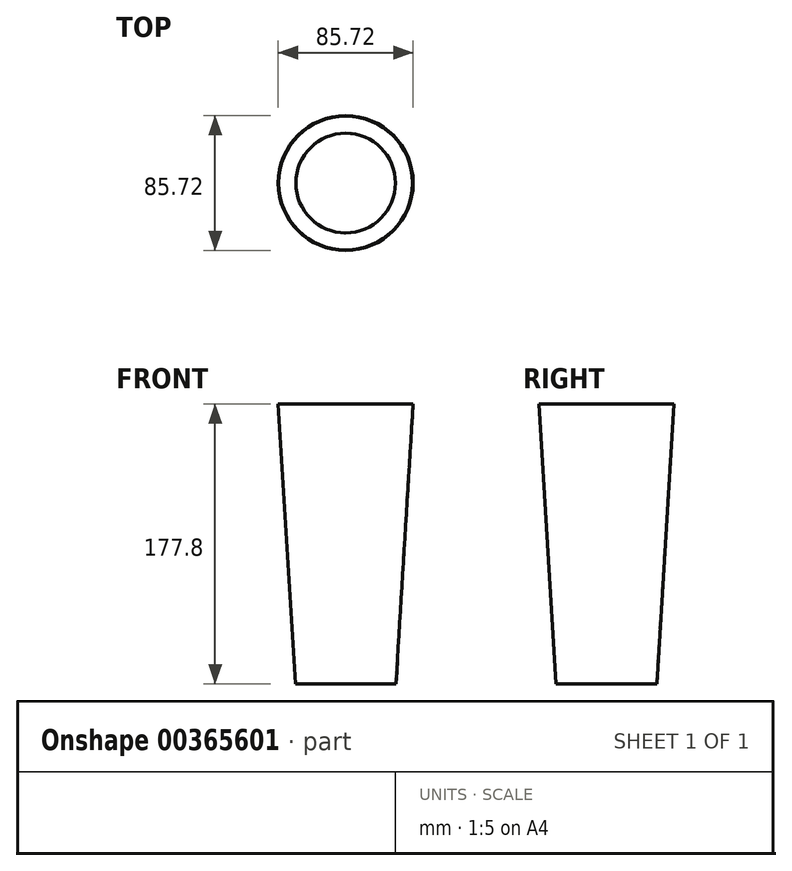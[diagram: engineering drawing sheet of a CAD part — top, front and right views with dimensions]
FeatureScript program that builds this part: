
annotation { "Feature Type Name" : "Feature", "Feature Type Description" : "" }
export const myFeature = defineFeature(function(context is Context, id is Id, definition is map)
    precondition{}
    {
        {
            var Q0;
            Q0=qCreatedBy(makeId("Top.planeOp"),FACE);
            var sketch = newSketch(context, id + "F0", { "sketchPlane" : qUnion([Q0])});
            skCircle(sketch, "E0", {"center": v(0, 0) * mm, "radius": 42.86 * mm});
            skSolve(sketch);
        }
        {
            var Q0;
            Q0=makeQuery(id+"F0.imprint","IMPRINT",FACE,{"disambiguationData":[TD([[makeQuery(id+"F0.imprint","IMPRINT",EDGE,{"derivedFrom":sQuery(id+"F0.wireOp",EDGE,"E0")}),1.0]])]});
            extrude(context, id + "F1", {"entities" : qUnion([Q0]), "oppositeDirection" : true, "depth" : 177.8 * mm, "offsetDistance" : 25.4 * mm, "hasDraft" : true, "draftAngle" : 3.5 * degree, "draftPullDirection" : true});
        }
        {
            var Q0;
            Q0=makeQuery(id+"F1.opExtrude","CAP_FACE",FACE,{"disambiguationData":[OSD([sQuery(id+"F0.wireOp",EDGE,"E0")])],"isStart":true});
            shell(context, id + "F2", {"entities" : qUnion([Q0]), "thickness" : 0.38 * mm});
        }
    });
